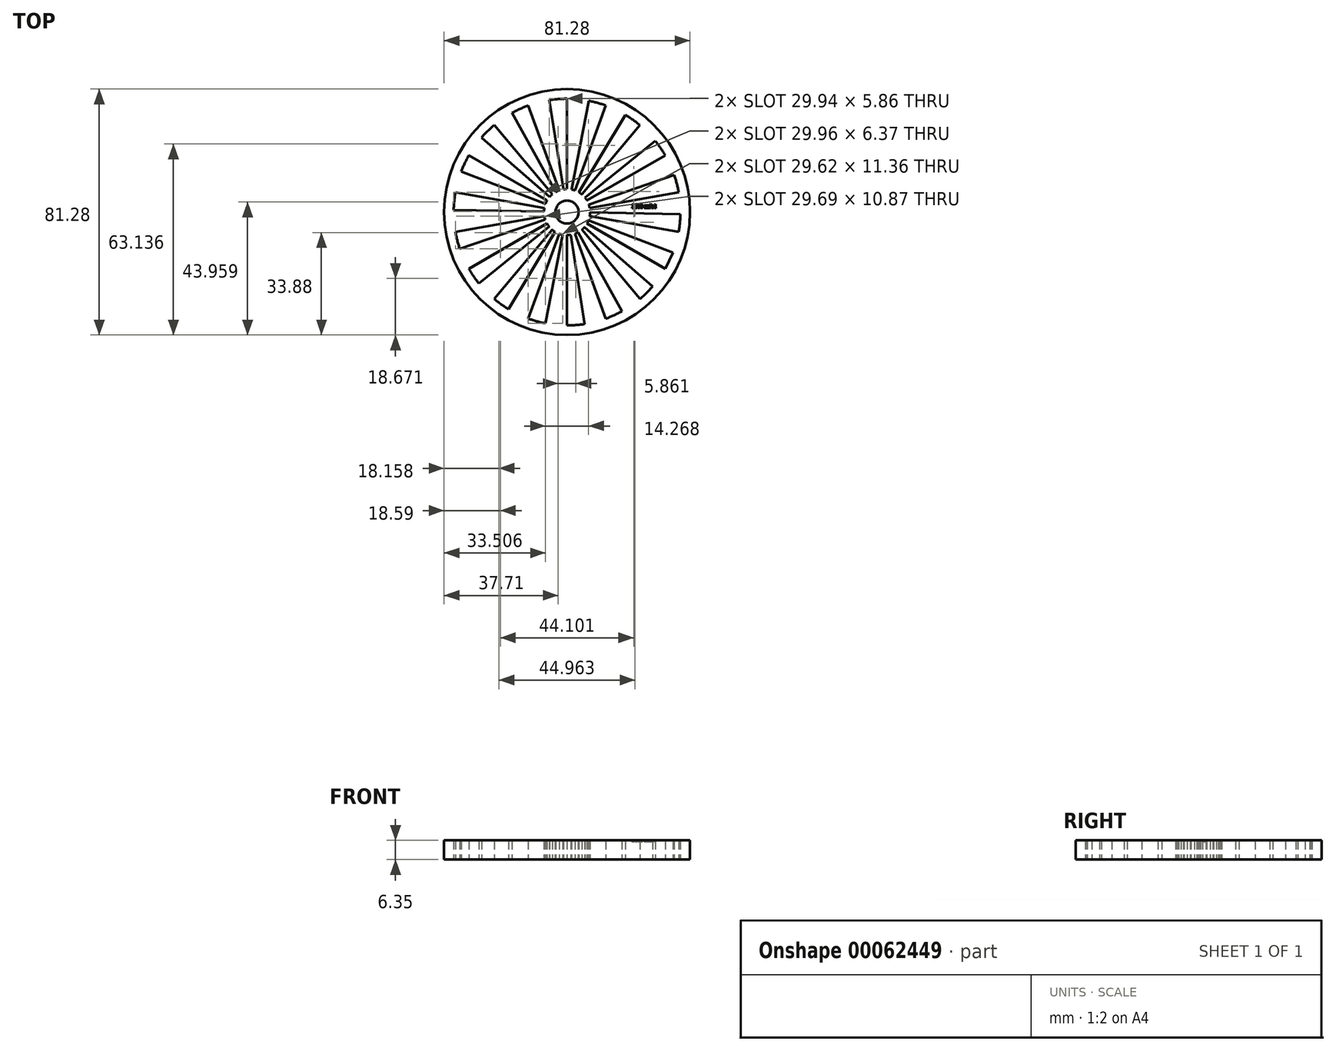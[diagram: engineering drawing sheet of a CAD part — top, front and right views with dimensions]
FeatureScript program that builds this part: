
annotation { "Feature Type Name" : "Feature", "Feature Type Description" : "" }
export const myFeature = defineFeature(function(context is Context, id is Id, definition is map)
    precondition{}
    {
        {
            var Q0;
            Q0=qCreatedBy(makeId("Top.planeOp"),FACE);
            var sketch = newSketch(context, id + "F0", { "sketchPlane" : qUnion([Q0])});
            skCircle(sketch, "E0", {"center": v(0, 0) * mm, "radius": 40.64 * mm});
            skCircle(sketch, "E1", {"center": v(0, 0) * mm, "radius": 3.8 * mm});
            skSolve(sketch);
        }
        {
            var Q0;
            Q0 = qSketchRegion(id + "F0", true);
            extrude(context, id + "F1", {"entities" : qUnion([Q0]), "offsetDistance" : 25.4 * mm, "depth" : 6.35 * mm});
        }
        {
            var Q0;
            Q0=qCreatedBy(makeId("Top.planeOp"),FACE);
            var sketch = newSketch(context, id + "F2", { "sketchPlane" : qUnion([Q0])});
            skLineSegment(sketch, "E2", {"start": v(1.2, -7.53) * mm, "end": v(5.86, -37) * mm});
            skArc(sketch, "E3", {"start": v(0, -37.47) * mm, "mid": v(2.94, -37.35) * mm, "end": v(5.86, -37) * mm});
            skLineSegment(sketch, "E4", {"start": v(0, -7.62) * mm, "end": v(0, -37.47) * mm});
            skArc(sketch, "E5", {"start": v(0, -7.62) * mm, "mid": v(0.6, -7.6) * mm, "end": v(1.2, -7.53) * mm});
            skLineSegment(sketch, "E6.1.0", {"start": v(-1.45, -7.48) * mm, "end": v(-7.15, -36.78) * mm});
            skArc(sketch, "E6.1.1", {"start": v(-12.81, -35.2) * mm, "mid": v(-10.01, -36.1) * mm, "end": v(-7.15, -36.78) * mm});
            skLineSegment(sketch, "E6.1.2", {"start": v(-2.6, -7.16) * mm, "end": v(-12.81, -35.2) * mm});
            skArc(sketch, "E6.1.3", {"start": v(-2.6, -7.16) * mm, "mid": v(-2.04, -7.34) * mm, "end": v(-1.45, -7.48) * mm});
            skLineSegment(sketch, "E6.2.0", {"start": v(-3.92, -6.53) * mm, "end": v(-19.3, -32.11) * mm});
            skArc(sketch, "E6.2.1", {"start": v(-24.08, -28.7) * mm, "mid": v(-21.76, -30.5) * mm, "end": v(-19.3, -32.11) * mm});
            skLineSegment(sketch, "E6.2.2", {"start": v(-4.9, -5.84) * mm, "end": v(-24.08, -28.7) * mm});
            skArc(sketch, "E6.2.3", {"start": v(-4.9, -5.84) * mm, "mid": v(-4.42, -6.2) * mm, "end": v(-3.92, -6.53) * mm});
            skLineSegment(sketch, "E6.3.0", {"start": v(-5.92, -4.8) * mm, "end": v(-29.12, -23.58) * mm});
            skArc(sketch, "E6.3.1", {"start": v(-32.45, -18.73) * mm, "mid": v(-30.88, -21.22) * mm, "end": v(-29.12, -23.58) * mm});
            skLineSegment(sketch, "E6.3.2", {"start": v(-6.6, -3.8) * mm, "end": v(-32.45, -18.73) * mm});
            skArc(sketch, "E6.3.3", {"start": v(-6.6, -3.8) * mm, "mid": v(-6.28, -4.32) * mm, "end": v(-5.92, -4.8) * mm});
            skLineSegment(sketch, "E6.4.0", {"start": v(-7.2, -2.48) * mm, "end": v(-35.42, -12.2) * mm});
            skArc(sketch, "E6.4.1", {"start": v(-36.9, -6.5) * mm, "mid": v(-36.27, -9.38) * mm, "end": v(-35.42, -12.2) * mm});
            skLineSegment(sketch, "E6.4.2", {"start": v(-7.5, -1.32) * mm, "end": v(-36.9, -6.5) * mm});
            skArc(sketch, "E6.4.3", {"start": v(-7.5, -1.32) * mm, "mid": v(-7.38, -1.9) * mm, "end": v(-7.2, -2.48) * mm});
            skLineSegment(sketch, "E6.5.0", {"start": v(-7.62, 0.13) * mm, "end": v(-37.46, 0.65) * mm});
            skArc(sketch, "E6.5.1", {"start": v(-36.9, 6.5) * mm, "mid": v(-37.3, 3.6) * mm, "end": v(-37.46, 0.65) * mm});
            skLineSegment(sketch, "E6.5.2", {"start": v(-7.5, 1.32) * mm, "end": v(-36.9, 6.5) * mm});
            skArc(sketch, "E6.5.3", {"start": v(-7.5, 1.32) * mm, "mid": v(-7.58, 0.73) * mm, "end": v(-7.62, 0.13) * mm});
            skLineSegment(sketch, "E6.6.0", {"start": v(-7.11, 2.73) * mm, "end": v(-34.98, 13.43) * mm});
            skArc(sketch, "E6.6.1", {"start": v(-32.45, 18.73) * mm, "mid": v(-33.82, 16.13) * mm, "end": v(-34.98, 13.43) * mm});
            skLineSegment(sketch, "E6.6.2", {"start": v(-6.6, 3.8) * mm, "end": v(-32.45, 18.73) * mm});
            skArc(sketch, "E6.6.3", {"start": v(-6.6, 3.8) * mm, "mid": v(-6.88, 3.28) * mm, "end": v(-7.11, 2.73) * mm});
            skLineSegment(sketch, "E6.7.0", {"start": v(-5.75, 5) * mm, "end": v(-28.28, 24.58) * mm});
            skArc(sketch, "E6.7.1", {"start": v(-24.08, 28.7) * mm, "mid": v(-26.26, 26.72) * mm, "end": v(-28.28, 24.58) * mm});
            skLineSegment(sketch, "E6.7.2", {"start": v(-4.9, 5.84) * mm, "end": v(-24.08, 28.7) * mm});
            skArc(sketch, "E6.7.3", {"start": v(-4.9, 5.84) * mm, "mid": v(-5.34, 5.43) * mm, "end": v(-5.75, 5) * mm});
            skLineSegment(sketch, "E6.8.0", {"start": v(-3.7, 6.66) * mm, "end": v(-18.16, 32.77) * mm});
            skArc(sketch, "E6.8.1", {"start": v(-12.81, 35.2) * mm, "mid": v(-15.54, 34.1) * mm, "end": v(-18.16, 32.77) * mm});
            skLineSegment(sketch, "E6.8.2", {"start": v(-2.6, 7.16) * mm, "end": v(-12.81, 35.2) * mm});
            skArc(sketch, "E6.8.3", {"start": v(-2.6, 7.16) * mm, "mid": v(-3.16, 6.93) * mm, "end": v(-3.7, 6.66) * mm});
            skLineSegment(sketch, "E6.9.0", {"start": v(-1.2, 7.53) * mm, "end": v(-5.86, 37) * mm});
            skArc(sketch, "E6.9.1", {"start": v(0, 37.47) * mm, "mid": v(-2.94, 37.35) * mm, "end": v(-5.86, 37) * mm});
            skLineSegment(sketch, "E6.9.2", {"start": v(0, 7.62) * mm, "end": v(0, 37.47) * mm});
            skArc(sketch, "E6.9.3", {"start": v(0, 7.62) * mm, "mid": v(-0.6, 7.6) * mm, "end": v(-1.2, 7.53) * mm});
            skLineSegment(sketch, "E6.anchor1", {"start": v(0, 0) * mm, "end": v(5.86, -37) * mm, "construction": true});
            skLineSegment(sketch, "E6.anchor2", {"start": v(0, 0) * mm, "end": v(-5.86, 37) * mm, "construction": true});
            skLineSegment(sketch, "E7.1.0", {"start": v(5.92, 4.8) * mm, "end": v(29.12, 23.58) * mm});
            skLineSegment(sketch, "E7.1.1", {"start": v(6.6, 3.8) * mm, "end": v(32.45, 18.73) * mm});
            skArc(sketch, "E7.1.2", {"start": v(6.6, 3.8) * mm, "mid": v(6.28, 4.32) * mm, "end": v(5.92, 4.8) * mm});
            skArc(sketch, "E7.1.3", {"start": v(32.45, 18.73) * mm, "mid": v(30.88, 21.22) * mm, "end": v(29.12, 23.58) * mm});
            skLineSegment(sketch, "E7.1.4", {"start": v(7.62, -0.13) * mm, "end": v(37.46, -0.65) * mm});
            skLineSegment(sketch, "E7.1.5", {"start": v(6.6, -3.8) * mm, "end": v(32.45, -18.73) * mm});
            skLineSegment(sketch, "E7.1.6", {"start": v(7.5, -1.32) * mm, "end": v(36.9, -6.5) * mm});
            skLineSegment(sketch, "E7.1.7", {"start": v(7.11, -2.73) * mm, "end": v(34.98, -13.43) * mm});
            skLineSegment(sketch, "E7.1.9", {"start": v(4.9, -5.84) * mm, "end": v(24.08, -28.7) * mm});
            skLineSegment(sketch, "E7.1.12", {"start": v(5.75, -5) * mm, "end": v(28.28, -24.58) * mm});
            skLineSegment(sketch, "E7.1.14", {"start": v(2.6, -7.16) * mm, "end": v(12.81, -35.2) * mm});
            skLineSegment(sketch, "E7.1.17", {"start": v(3.7, -6.66) * mm, "end": v(18.16, -32.77) * mm});
            skArc(sketch, "E7.1.19", {"start": v(24.08, -28.7) * mm, "mid": v(26.26, -26.72) * mm, "end": v(28.28, -24.58) * mm});
            skArc(sketch, "E7.1.21", {"start": v(12.81, -35.2) * mm, "mid": v(15.54, -34.1) * mm, "end": v(18.16, -32.77) * mm});
            skLineSegment(sketch, "E7.2.1", {"start": v(-6.6, 3.81) * mm, "end": v(-32.45, 18.73) * mm});
            skArc(sketch, "E7.2.2", {"start": v(-6.6, 3.81) * mm, "mid": v(-6.88, 3.28) * mm, "end": v(-7.11, 2.73) * mm});
            skLineSegment(sketch, "E7.2.8", {"start": v(7.5, -1.32) * mm, "end": v(36.9, -6.5) * mm});
            skLineSegment(sketch, "E7.2.9", {"start": v(2.6, 7.16) * mm, "end": v(12.81, 35.2) * mm});
            skLineSegment(sketch, "E7.2.10", {"start": v(6.6, 3.8) * mm, "end": v(32.45, 18.73) * mm});
            skLineSegment(sketch, "E7.2.11", {"start": v(5.92, 4.8) * mm, "end": v(29.12, 23.58) * mm});
            skLineSegment(sketch, "E7.2.12", {"start": v(1.45, 7.48) * mm, "end": v(7.15, 36.78) * mm});
            skLineSegment(sketch, "E7.2.13", {"start": v(7.62, -0.13) * mm, "end": v(37.46, -0.65) * mm});
            skLineSegment(sketch, "E7.2.14", {"start": v(4.9, 5.84) * mm, "end": v(24.08, 28.7) * mm});
            skLineSegment(sketch, "E7.2.15", {"start": v(7.5, 1.32) * mm, "end": v(36.9, 6.5) * mm});
            skLineSegment(sketch, "E7.2.16", {"start": v(7.2, 2.48) * mm, "end": v(35.42, 12.2) * mm});
            skLineSegment(sketch, "E7.2.17", {"start": v(3.92, 6.53) * mm, "end": v(19.3, 32.11) * mm});
            skArc(sketch, "E7.2.18", {"start": v(36.9, -6.5) * mm, "mid": v(37.3, -3.6) * mm, "end": v(37.46, -0.65) * mm});
            skArc(sketch, "E7.2.19", {"start": v(12.81, 35.2) * mm, "mid": v(10.01, 36.1) * mm, "end": v(7.15, 36.78) * mm});
            skArc(sketch, "E7.2.20", {"start": v(32.45, 18.73) * mm, "mid": v(30.88, 21.22) * mm, "end": v(29.12, 23.58) * mm});
            skArc(sketch, "E7.2.21", {"start": v(24.08, 28.7) * mm, "mid": v(21.76, 30.5) * mm, "end": v(19.3, 32.11) * mm});
            skArc(sketch, "E7.2.22", {"start": v(36.9, 6.5) * mm, "mid": v(36.27, 9.38) * mm, "end": v(35.42, 12.2) * mm});
            skArc(sketch, "E8.trimOffspring", {"start": v(2.6, 7.16) * mm, "mid": v(2.04, 7.34) * mm, "end": v(1.45, 7.48) * mm});
            skArc(sketch, "E9.trimOffspring", {"start": v(4.9, 5.84) * mm, "mid": v(4.42, 6.2) * mm, "end": v(3.92, 6.53) * mm});
            skArc(sketch, "E10.trimOffspring", {"start": v(7.5, 1.32) * mm, "mid": v(7.38, 1.9) * mm, "end": v(7.2, 2.48) * mm});
            skArc(sketch, "E11.trimOffspring", {"start": v(7.5, -1.32) * mm, "mid": v(7.58, -0.73) * mm, "end": v(7.62, -0.13) * mm});
            skArc(sketch, "E12.trimOffspring", {"start": v(6.6, -3.8) * mm, "mid": v(6.88, -3.28) * mm, "end": v(7.11, -2.73) * mm});
            skArc(sketch, "E13.trimOffspring", {"start": v(4.9, -5.84) * mm, "mid": v(5.34, -5.43) * mm, "end": v(5.75, -5) * mm});
            skArc(sketch, "E14.trimOffspring", {"start": v(2.6, -7.16) * mm, "mid": v(3.16, -6.93) * mm, "end": v(3.7, -6.66) * mm});
            skLineSegment(sketch, "E15", {"start": v(34.98, -13.43) * mm, "end": v(32.45, -18.73) * mm});
            skSolve(sketch);
        }
        {
            var Q0;
            Q0 = qSketchRegion(id + "F2", true);
            extrude(context, id + "F3", {"entities" : qUnion([Q0]), "operationType" : NewBodyOperationType.REMOVE, "depth" : 25.4 * mm});
        }
        {
            var Q0;
            Q0=makeQuery(id+"F1.opExtrude","CAP_FACE",FACE,{"disambiguationData":[OSD([sQuery(id+"F0.wireOp",EDGE,"E0"),sQuery(id+"F0.wireOp",EDGE,"E1")])],"isStart":false});
            var sketch = newSketch(context, id + "F4", { "sketchPlane" : qUnion([Q0])});
            skText(sketch, "E16", { "text": "2016 mlb1", "fontName": "RobotoSlab-Regular.ttf"});
            const initialGuessF4  = {"E16": [0.02135, 0.00128, 1, 0, 0.00128]};
            skSetInitialGuess(sketch, initialGuessF4);
            skSolve(sketch);
        }
        {
            var Q0;
            Q0 = qSketchRegion(id + "F4", true);
            extrude(context, id + "F5", {"entities" : qUnion([Q0]), "operationType" : NewBodyOperationType.REMOVE, "oppositeDirection" : true, "offsetDistance" : 25.4 * mm, "depth" : 0.5 * mm});
        }
    });
